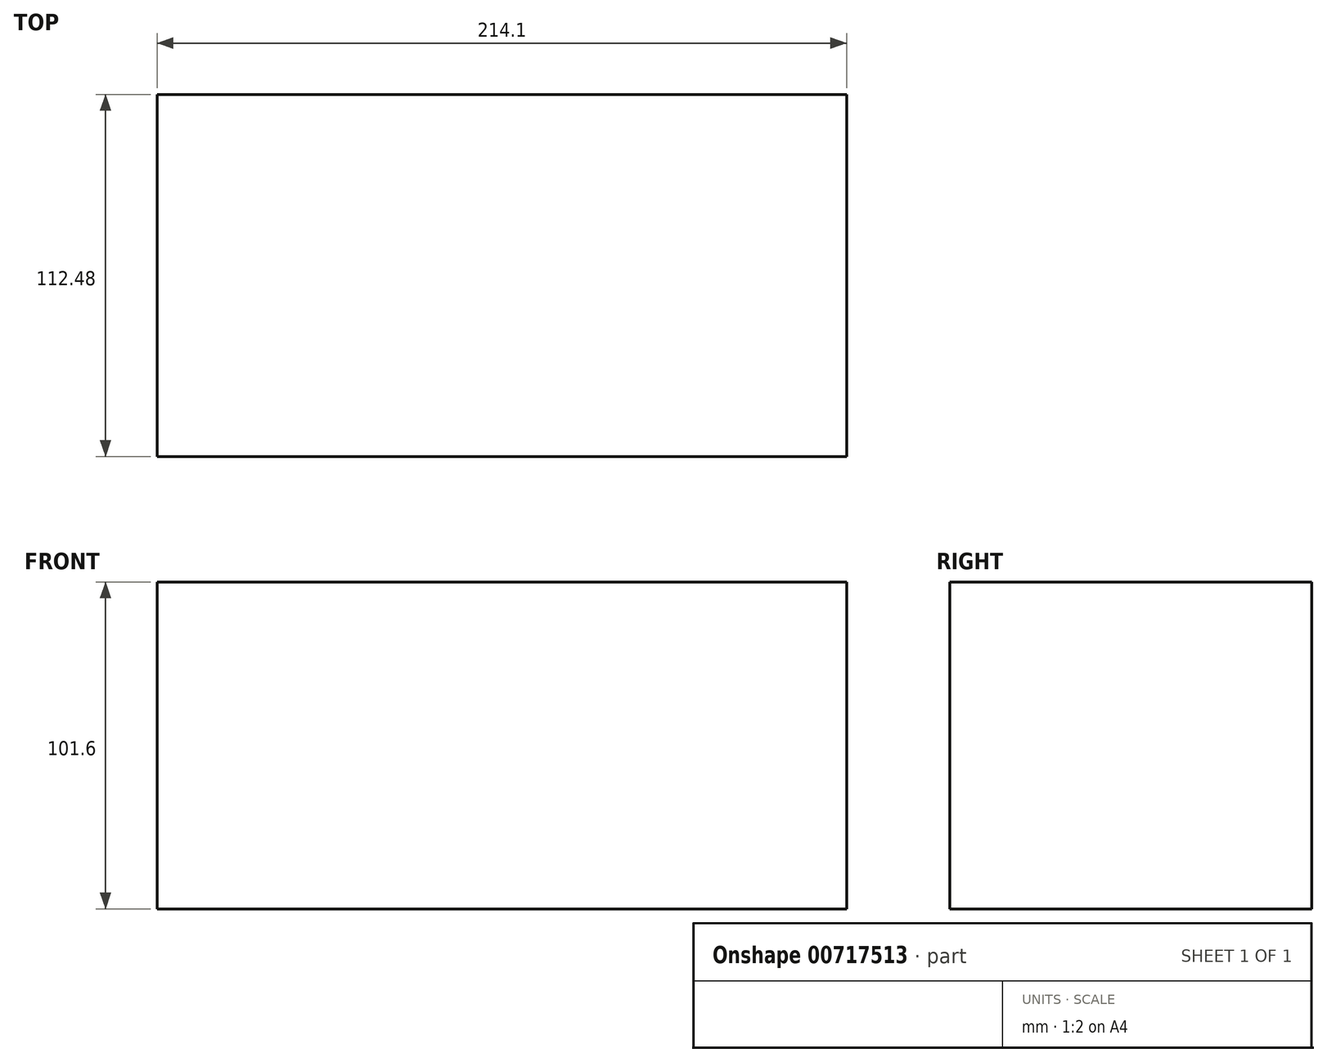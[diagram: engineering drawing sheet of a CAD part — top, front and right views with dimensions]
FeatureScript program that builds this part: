
annotation { "Feature Type Name" : "Feature", "Feature Type Description" : "" }
export const myFeature = defineFeature(function(context is Context, id is Id, definition is map)
    precondition{}
    {
        {
            var Q0;
            Q0=qCreatedBy(makeId("Top.planeOp"),FACE);
            var sketch = newSketch(context, id + "F0", { "sketchPlane" : qUnion([Q0])});
            skLineSegment(sketch, "E0.bottom", {"start": v(107.05, 56.24) * mm, "end": v(-107.05, 56.24) * mm});
            skLineSegment(sketch, "E0.top", {"start": v(107.05, -56.24) * mm, "end": v(-107.05, -56.24) * mm});
            skLineSegment(sketch, "E0.left", {"start": v(107.05, 56.24) * mm, "end": v(107.05, -56.24) * mm});
            skLineSegment(sketch, "E0.right", {"start": v(-107.05, 56.24) * mm, "end": v(-107.05, -56.24) * mm});
            skPoint(sketch, "E0.middle", {"position": v(0, 0) * mm});
            skSolve(sketch);
        }
        {
            var Q0;
            Q0=makeQuery(id+"F0.imprint","IMPRINT",FACE,{"disambiguationData":[TD([[makeQuery(id+"F0.imprint","IMPRINT",EDGE,{"derivedFrom":sQuery(id+"F0.wireOp",EDGE,"E0.bottom")}),1.0]])]});
            extrude(context, id + "F1", {"entities" : qUnion([Q0]), "depth" : 101.6 * mm, "offsetDistance" : 25.4 * mm});
        }
    });
